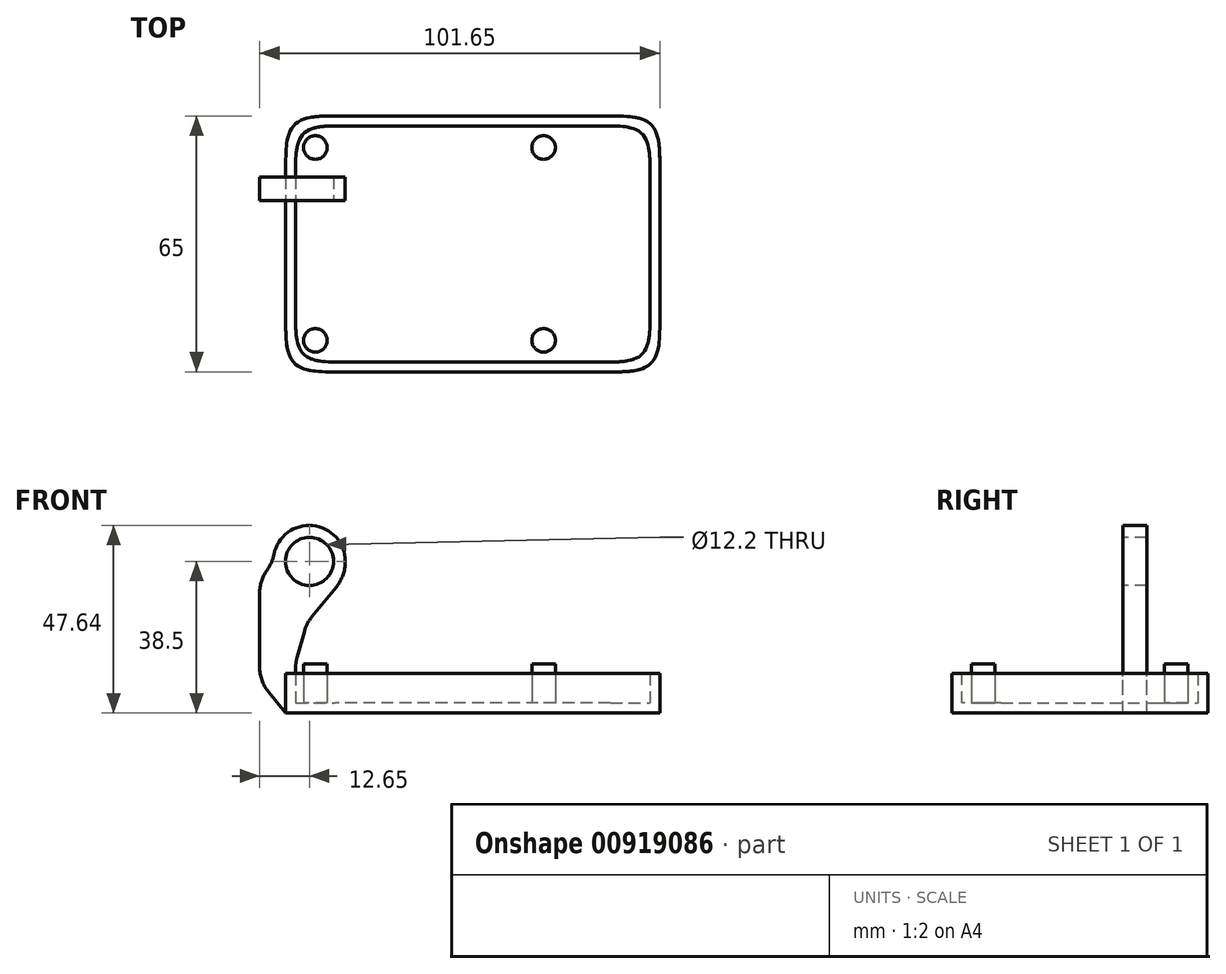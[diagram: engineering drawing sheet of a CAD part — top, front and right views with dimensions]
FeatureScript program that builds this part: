
annotation { "Feature Type Name" : "Feature", "Feature Type Description" : "" }
export const myFeature = defineFeature(function(context is Context, id is Id, definition is map)
    precondition{}
    {
        {
            var Q0;
            Q0=qCreatedBy(makeId("Top.planeOp"),FACE);
            var sketch = newSketch(context, id + "F0", { "sketchPlane" : qUnion([Q0])});
            skLineSegment(sketch, "E0.bottom", {"start": v(45, -30) * mm, "end": v(-45, -30) * mm});
            skLineSegment(sketch, "E0.top", {"start": v(45, 30) * mm, "end": v(-45, 30) * mm});
            skLineSegment(sketch, "E0.left", {"start": v(45, -30) * mm, "end": v(45, 30) * mm});
            skLineSegment(sketch, "E0.right", {"start": v(-45, -30) * mm, "end": v(-45, 30) * mm});
            skPoint(sketch, "E0.middle", {"position": v(0, 0) * mm});
            skSolve(sketch);
        }
        {
            var Q0;
            Q0 = qSketchRegion(id + "F0", true);
            extrude(context, id + "F1", {"entities" : qUnion([Q0]), "depth" : 2.5 * mm, "offsetDistance" : 25 * mm});
        }
        {
            var Q0;
            Q0=qCreatedBy(makeId("Top.planeOp"),FACE);
            var sketch = newSketch(context, id + "F2", { "sketchPlane" : qUnion([Q0])});
            skLineSegment(sketch, "E1.0.0", {"start": v(45, -30) * mm, "end": v(45, 30) * mm});
            skLineSegment(sketch, "E1.0.1", {"start": v(45, 30) * mm, "end": v(-45, 30) * mm});
            skLineSegment(sketch, "E1.0.2", {"start": v(-45, 30) * mm, "end": v(-45, -30) * mm});
            skLineSegment(sketch, "E1.0.3", {"start": v(-45, -30) * mm, "end": v(45, -30) * mm});
            skLineSegment(sketch, "E2.0", {"start": v(47.5, -32.5) * mm, "end": v(47.5, 32.5) * mm});
            skLineSegment(sketch, "E2.1", {"start": v(-47.5, -32.5) * mm, "end": v(47.5, -32.5) * mm});
            skLineSegment(sketch, "E2.2", {"start": v(-47.5, 32.5) * mm, "end": v(-47.5, -32.5) * mm});
            skLineSegment(sketch, "E2.3", {"start": v(47.5, 32.5) * mm, "end": v(-47.5, 32.5) * mm});
            skSolve(sketch);
        }
        {
            var Q0;
            Q0 = qSketchRegion(id + "F2", true);
            extrude(context, id + "F3", {"entities" : qUnion([Q0]), "operationType" : NewBodyOperationType.ADD, "depth" : 10 * mm, "offsetDistance" : 25 * mm});
        }
        {
            var Q0;
            Q0=makeQuery(id+"F3.opExtrude","SWEPT_EDGE",EDGE,{"disambiguationData":[OSD([sQuery(id+"F2.wireOp",EDGE,"E1.0.1"),sQuery(id+"F2.wireOp",EDGE,"E1.0.2")])]});
            var Q1;
            Q1=makeQuery(id+"F3.opExtrude","SWEPT_EDGE",EDGE,{"disambiguationData":[OSD([sQuery(id+"F2.wireOp",EDGE,"E1.0.0"),sQuery(id+"F2.wireOp",EDGE,"E1.0.1")])]});
            var Q2;
            Q2=makeQuery(id+"F3.opExtrude","SWEPT_EDGE",EDGE,{"disambiguationData":[OSD([sQuery(id+"F2.wireOp",EDGE,"E1.0.0"),sQuery(id+"F2.wireOp",EDGE,"E1.0.3")])]});
            var Q3;
            Q3=makeQuery(id+"F3.opExtrude","SWEPT_EDGE",EDGE,{"disambiguationData":[OSD([sQuery(id+"F2.wireOp",EDGE,"E1.0.2"),sQuery(id+"F2.wireOp",EDGE,"E1.0.3")])]});
            fillet(context, id + "F4", {"entities" : qUnion([Q0, Q1, Q2, Q3]), "radius" : 10 * mm, "tangentPropagation" : true, "rho" : 0.6, "crossSection" : FilletCrossSection.CONIC, "allowEdgeOverflow" : false});
        }
        {
            var Q0;
            Q0=makeQuery(id+"F3.opExtrude","SWEPT_EDGE",EDGE,{"disambiguationData":[OSD([sQuery(id+"F2.wireOp",EDGE,"E2.2"),sQuery(id+"F2.wireOp",EDGE,"E2.3")])]});
            var Q1;
            Q1=makeQuery(id+"F3.opExtrude","SWEPT_EDGE",EDGE,{"disambiguationData":[OSD([sQuery(id+"F2.wireOp",EDGE,"E2.1"),sQuery(id+"F2.wireOp",EDGE,"E2.2")])]});
            var Q2;
            Q2=makeQuery(id+"F3.opExtrude","SWEPT_EDGE",EDGE,{"disambiguationData":[OSD([sQuery(id+"F2.wireOp",EDGE,"E2.0"),sQuery(id+"F2.wireOp",EDGE,"E2.3")])]});
            var Q3;
            Q3=makeQuery(id+"F3.opExtrude","SWEPT_EDGE",EDGE,{"disambiguationData":[OSD([sQuery(id+"F2.wireOp",EDGE,"E2.0"),sQuery(id+"F2.wireOp",EDGE,"E2.1")])]});
            fillet(context, id + "F5", {"entities" : qUnion([Q0, Q1, Q2, Q3]), "radius" : 11 * mm, "tangentPropagation" : true, "rho" : 0.6, "crossSection" : FilletCrossSection.CONIC, "allowEdgeOverflow" : false});
        }
        {
            var Q0;
            Q0=makeQuery(id+"F1.opExtrude","CAP_FACE",FACE,{"disambiguationData":[OSD([sQuery(id+"F0.wireOp",EDGE,"E0.bottom"),sQuery(id+"F0.wireOp",EDGE,"E0.top"),sQuery(id+"F0.wireOp",EDGE,"E0.left"),sQuery(id+"F0.wireOp",EDGE,"E0.right")])],"isStart":false});
            var sketch = newSketch(context, id + "F6", { "sketchPlane" : qUnion([Q0])});
            skCircle(sketch, "E3", {"center": v(-40, 24.5) * mm, "radius": 3 * mm});
            skCircle(sketch, "E4", {"center": v(-40, -24.5) * mm, "radius": 3 * mm});
            skCircle(sketch, "E5", {"center": v(18, -24.5) * mm, "radius": 3 * mm});
            skCircle(sketch, "E6", {"center": v(18, 24.5) * mm, "radius": 3 * mm});
            skLineSegment(sketch, "E7.bottom", {"start": v(-40, 24.5) * mm, "end": v(18, 24.5) * mm, "construction": true});
            skLineSegment(sketch, "E7.top", {"start": v(-40, -24.5) * mm, "end": v(18, -24.5) * mm, "construction": true});
            skLineSegment(sketch, "E7.left", {"start": v(-40, 24.5) * mm, "end": v(-40, -24.5) * mm, "construction": true});
            skLineSegment(sketch, "E7.right", {"start": v(18, 24.5) * mm, "end": v(18, -24.5) * mm, "construction": true});
            skLineSegment(sketch, "E8", {"start": v(-40, 0) * mm, "end": v(0, 0) * mm, "construction": true});
            skSolve(sketch);
        }
        {
            var Q0;
            Q0 = qSketchRegion(id + "F6", true);
            extrude(context, id + "F7", {"entities" : qUnion([Q0]), "operationType" : NewBodyOperationType.ADD, "depth" : 10 * mm, "offsetDistance" : 25 * mm});
        }
        {
            var Q0;
            Q0=makeQuery(id+"F3.opExtrude","CAP_FACE",FACE,{"disambiguationData":[OSD([sQuery(id+"F2.wireOp",EDGE,"E1.0.0"),sQuery(id+"F2.wireOp",EDGE,"E1.0.1"),sQuery(id+"F2.wireOp",EDGE,"E1.0.2"),sQuery(id+"F2.wireOp",EDGE,"E1.0.3"),sQuery(id+"F2.wireOp",EDGE,"E2.0"),sQuery(id+"F2.wireOp",EDGE,"E2.1"),sQuery(id+"F2.wireOp",EDGE,"E2.2"),sQuery(id+"F2.wireOp",EDGE,"E2.3")])],"isStart":false});
            var sketch = newSketch(context, id + "F8", { "sketchPlane" : qUnion([Q0])});
            skLineSegment(sketch, "E9", {"start": v(-5, -32.5) * mm, "end": v(-5, -30) * mm});
            skLineSegment(sketch, "E10", {"start": v(-5, -30) * mm, "end": v(-35, -30) * mm});
            skFitSpline(sketch, "E11.0", {"points": [v(-35, -30) * mm, v(-36.69, -30) * mm, v(-38.09, -29.9) * mm, v(-39.21, -29.7) * mm, v(-39.99, -29.57) * mm, v(-40.67, -29.38) * mm, v(-41.25, -29.14) * mm, v(-41.95, -28.85) * mm, v(-42.54, -28.47) * mm, v(-43, -28) * mm, v(-43.48, -27.52) * mm, v(-43.86, -26.93) * mm, v(-44.15, -26.23) * mm, v(-44.39, -25.65) * mm, v(-44.57, -24.98) * mm, v(-44.7, -24.2) * mm, v(-44.9, -23.08) * mm, v(-45, -21.68) * mm, v(-45, -20) * mm]});
            skFitSpline(sketch, "E12.0", {"points": [v(-47.5, -21.5) * mm, v(-47.5, -23.35) * mm, v(-47.4, -24.9) * mm, v(-47.18, -26.13) * mm, v(-47.03, -26.99) * mm, v(-46.82, -27.73) * mm, v(-46.56, -28.37) * mm, v(-46.23, -29.14) * mm, v(-45.81, -29.79) * mm, v(-45.3, -30.3) * mm, v(-44.77, -30.83) * mm, v(-44.13, -31.24) * mm, v(-43.35, -31.56) * mm, v(-42.72, -31.82) * mm, v(-41.98, -32.03) * mm, v(-41.12, -32.18) * mm, v(-39.9, -32.4) * mm, v(-38.35, -32.5) * mm, v(-36.5, -32.5) * mm]});
            skLineSegment(sketch, "E13", {"start": v(-5, -32.5) * mm, "end": v(-36.5, -32.5) * mm});
            skLineSegment(sketch, "E14", {"start": v(-45, -20) * mm, "end": v(-45, -16) * mm});
            skLineSegment(sketch, "E15", {"start": v(-45, -16) * mm, "end": v(-47.5, -16) * mm});
            skLineSegment(sketch, "E16", {"start": v(-47.5, -16) * mm, "end": v(-47.5, -21.5) * mm});
            skSolve(sketch);
        }
        {
            var Q0;
            Q0=makeQuery(id+"F3.opExtrude","SWEPT_FACE",FACE,{"disambiguationData":[OSD([sQuery(id+"F2.wireOp",EDGE,"E2.3")])]});
            cPlane(context, id + "F9", {"entities" : qUnion([Q0]), "cplaneType" : CPlaneType.OFFSET, "offset" : 21.5 * mm, "oppositeDirection" : true, "width" : 150 * mm, "height" : 150 * mm});
        }
        {
            var Q0;
            Q0=qCreatedBy(id+"F9.planeOp",FACE);
            var sketch = newSketch(context, id + "F10", { "sketchPlane" : qUnion([Q0])});
            skLineSegment(sketch, "E17", {"start": v(47.5, 0) * mm, "end": v(54.15, 8.09) * mm});
            skLineSegment(sketch, "E18", {"start": v(54.15, 8.09) * mm, "end": v(54.15, 33.6) * mm});
            skLineSegment(sketch, "E19", {"start": v(32.4, 38.5) * mm, "end": v(32.4, 34.8) * mm});
            skLineSegment(sketch, "E20", {"start": v(32.4, 34.8) * mm, "end": v(42.24, 22.75) * mm});
            skLineSegment(sketch, "E21", {"start": v(42.24, 22.75) * mm, "end": v(45, 12.83) * mm});
            skLineSegment(sketch, "E22", {"start": v(45, 12.83) * mm, "end": v(45, 0) * mm});
            skLineSegment(sketch, "E23", {"start": v(45, 0) * mm, "end": v(47.5, 0) * mm});
            skCircle(sketch, "E24", {"center": v(41.5, 38.5) * mm, "radius": 6.1 * mm});
            skLineSegment(sketch, "E25", {"start": v(54.15, 33.6) * mm, "end": v(50.69, 38.5) * mm});
            skLineSegment(sketch, "E26", {"start": v(41.5, 38.5) * mm, "end": v(50.69, 38.5) * mm, "construction": true});
            skLineSegment(sketch, "E27", {"start": v(32.4, 38.5) * mm, "end": v(41.5, 38.5) * mm, "construction": true});
            skArc(sketch, "E28", {"start": v(50.69, 38.5) * mm, "mid": v(41.54, 47.64) * mm, "end": v(32.4, 38.5) * mm});
            skSolve(sketch);
        }
        {
            var Q0;
            Q0 = qSketchRegion(id + "F10", true);
            extrude(context, id + "F11", {"entities" : qUnion([Q0]), "operationType" : NewBodyOperationType.ADD, "depth" : 6 * mm, "offsetDistance" : 25 * mm});
        }
        {
            var Q0;
            Q0=makeQuery(id+"F11.opExtrude","SWEPT_EDGE",EDGE,{"disambiguationData":[OSD([sQuery(id+"F10.wireOp",EDGE,"E19"),sQuery(id+"F10.wireOp",EDGE,"E20")])]});
            var Q1;
            Q1=makeQuery(id+"F11.opExtrude","SWEPT_EDGE",EDGE,{"disambiguationData":[OSD([sQuery(id+"F10.wireOp",EDGE,"E20"),sQuery(id+"F10.wireOp",EDGE,"E21")])]});
            var Q2;
            Q2=makeQuery(id+"F11.opExtrude","SWEPT_EDGE",EDGE,{"disambiguationData":[OSD([sQuery(id+"F10.wireOp",EDGE,"E21"),sQuery(id+"F10.wireOp",EDGE,"E22")])]});
            var Q3;
            Q3=makeQuery(id+"F11.opExtrude","SWEPT_EDGE",EDGE,{"disambiguationData":[OSD([sQuery(id+"F10.wireOp",EDGE,"E25"),sQuery(id+"F10.wireOp",EDGE,"E28")])]});
            var Q4;
            Q4=makeQuery(id+"F11.opExtrude","SWEPT_EDGE",EDGE,{"disambiguationData":[OSD([sQuery(id+"F10.wireOp",EDGE,"E18"),sQuery(id+"F10.wireOp",EDGE,"E25")])]});
            var Q5;
            Q5=makeQuery(id+"F11.opExtrude","SWEPT_EDGE",EDGE,{"disambiguationData":[OSD([sQuery(id+"F10.wireOp",EDGE,"E17"),sQuery(id+"F10.wireOp",EDGE,"E18")])]});
            fillet(context, id + "F12", {"entities" : qUnion([Q0, Q1, Q2, Q3, Q4, Q5]), "radius" : 10 * mm, "tangentPropagation" : true, "allowEdgeOverflow" : false});
        }
    });
